AUTODESK INVENTOR PART (.ipt)
format: ipt  version: 2021.1 (Build 251245010, 245A)  size: 531,456 bytes
history: native  units: mm
features: extrude x9, sketch x9, fillet x2, plane x1, loft x1, mirror x1
ambient origin geometry x8: Origin, YZ Plane, XZ Plane, XY Plane, X Axis, Y Axis, Z Axis, Center Point
bodies: Volumenkörper1 (feature_tree)
feature tree (23):
  extrude  "Extrusion1"  Depth=24.5mm
  extrude  "Extrusion2"  Depth=3.6mm
  extrude  "Extrusion3"  Depth=19.75mm
  extrude  "Extrusion4"  Depth=12.25mm
  sketch  "Skizze5"  dims[d8=0.0mm d9=4.0mm]
  extrude  "Extrusion5"  Depth=4.0mm
  extrude  "Extrusion7"  Depth=2.0mm
  extrude  "Extrusion8"  Depth=12.0mm
  extrude  "Extrusion6"  Depth=13.75mm
  plane  "Arbeitsebene1"
  extrude  "Extrusion9"  Depth=1.0mm TaperAngle=0.0deg
  loft  "Erhebung1"
  mirror  "Spiegeln1"
  fillet  "Rundung2"  Radius=2.0mm
  fillet  "Rundung3"  Radius=10.0mm
  sketch  "Skizze1"  dims[d0=31.5mm d1=24.5mm]
  sketch  "Skizze2"  dims[d2=4.5mm d3=3.6mm]
  sketch  "Skizze3"  dims[d4=39.5mm d5=19.75mm]
  sketch  "Skizze4"  dims[d6=15.75mm d7=12.25mm]
  sketch  "Skizze6"  dims[d10=37.0mm d11=0.0mm d13=2.0mm]
  sketch  "Skizze7"  dims[d14=10.0mm d15=0.0mm d16=12.0mm]
  sketch  "Skizze8"  dims[d17=20.0mm d18=13.75mm]
  sketch  "Skizze9"  dims[d19=39.5mm d20=5.0mm d21=0.0mm d22=2.0mm d23=2.0mm d24=10.0mm d25=0.0mm d26=3.6mm d27=2.0mm d28=8.0mm d29=5.826561mm d30=1.463907mm d31=98.0mm d32=25.0mm d33=12.5mm d34=5.5mm d35=5.5mm d36=29.0mm d37=14.5mm d38=200.0mm d39=200.0mm d40=11.0mm d41=11.0mm d42=39.5mm d43=19.75mm d44=15.0mm d45=10.0mm d46=0.0mm d47=10.0mm d48=0.0mm d49=10.0mm d50=0.0mm d51=10.0mm d52=0.0mm d53=5.0mm d54=37.0mm d55=18.5mm d56=4.0mm d57=15.0mm d58=0.0mm d59=10.0mm d60=16.0mm d61=13.5mm d62=0.0mm d63=90.0deg d64=0.0mm d65=90.0deg d66=1.0mm d67=1.0mm]
